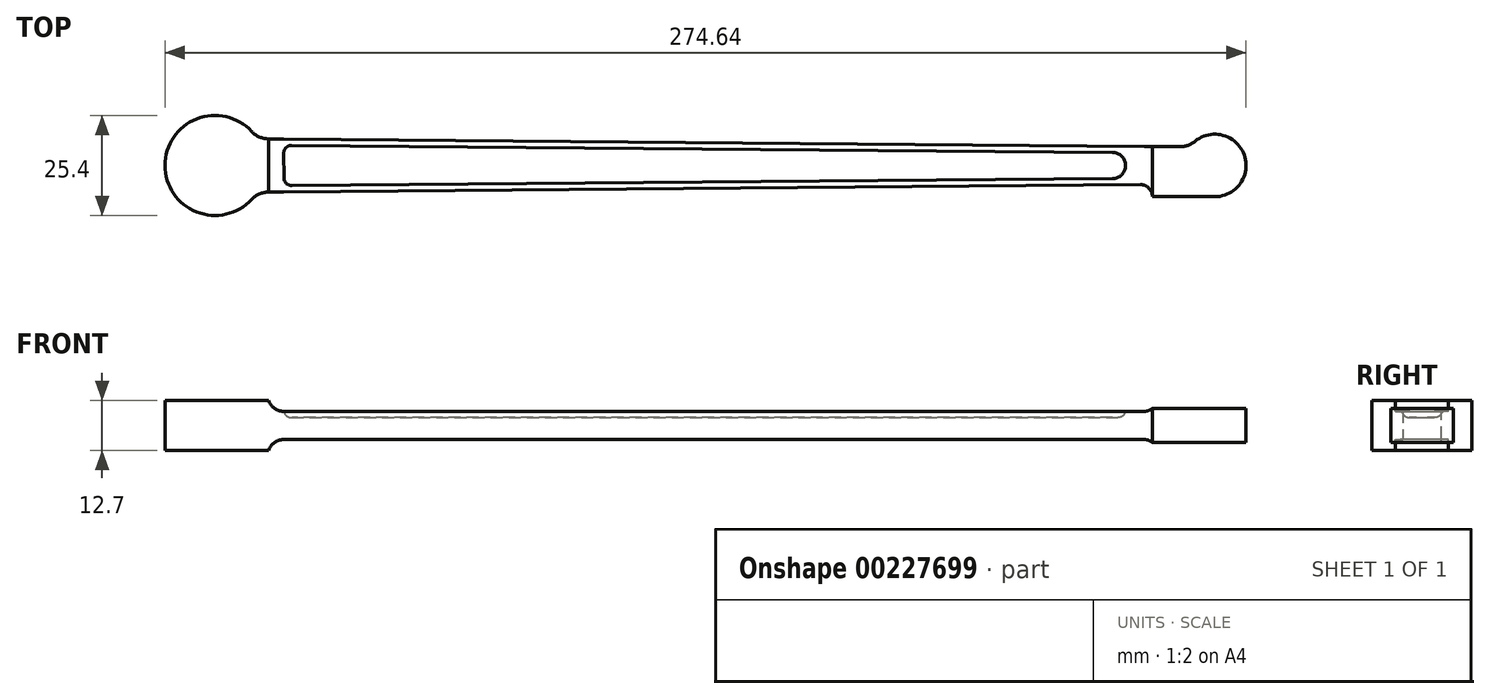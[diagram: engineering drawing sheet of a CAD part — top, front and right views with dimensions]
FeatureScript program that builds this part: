
annotation { "Feature Type Name" : "Feature", "Feature Type Description" : "" }
export const myFeature = defineFeature(function(context is Context, id is Id, definition is map)
    precondition{}
    {
        {
            var Q0;
            Q0=qCreatedBy(makeId("Top.planeOp"),FACE);
            var sketch = newSketch(context, id + "F0", { "sketchPlane" : qUnion([Q0])});
            skLineSegment(sketch, "E0", {"start": v(-127, 0) * mm, "end": v(127, 0) * mm, "construction": true});
            skArc(sketch, "E1", {"start": v(-117.7, 8.66) * mm, "mid": v(-139.7, 0) * mm, "end": v(-117.7, -8.66) * mm});
            skArc(sketch, "E2", {"start": v(127, -7.94) * mm, "mid": v(134.48, 2.67) * mm, "end": v(121.97, 6.14) * mm});
            skLineSegment(sketch, "E3", {"start": v(-113.37, 6.75) * mm, "end": v(118.12, 4.78) * mm});
            skLineSegment(sketch, "E4", {"start": v(-113.37, -6.75) * mm, "end": v(108.1, -4.87) * mm});
            skArc(sketch, "E5", {"start": v(-117.7, 8.66) * mm, "mid": v(-115.73, 7.26) * mm, "end": v(-113.37, 6.75) * mm});
            skArc(sketch, "E6", {"start": v(-113.37, -6.75) * mm, "mid": v(-115.73, -7.26) * mm, "end": v(-117.7, -8.66) * mm});
            skLineSegment(sketch, "E7", {"start": v(127, -7.94) * mm, "end": v(111.12, -7.94) * mm});
            skArc(sketch, "E8", {"start": v(111.13, -7.87) * mm, "mid": v(110.24, -5.74) * mm, "end": v(108.1, -4.87) * mm});
            skLineSegment(sketch, "E9", {"start": v(111.12, -7.87) * mm, "end": v(111.12, -7.94) * mm});
            skLineSegment(sketch, "E10", {"start": v(111.12, -7.87) * mm, "end": v(111.12, 4.84) * mm});
            skLineSegment(sketch, "E11", {"start": v(-113.37, 6.75) * mm, "end": v(-113.37, -6.75) * mm});
            skPoint(sketch, "E12.orphan", {"position": v(120.65, -4.76) * mm});
            skPoint(sketch, "E13.orphan", {"position": v(-116.26, 6.77) * mm});
            skPoint(sketch, "E14.orphan", {"position": v(-116.26, -6.77) * mm});
            skPoint(sketch, "E15.visualSharp", {"position": v(120.65, 4.76) * mm});
            skArc(sketch, "E15.filletArc", {"start": v(118.12, 4.78) * mm, "mid": v(120.16, 5.12) * mm, "end": v(121.97, 6.14) * mm});
            skSolve(sketch);
        }
        {
            var Q0;
            Q0=qSketchRegion(id+"F0",true);
            extrude(context, id + "F1", {"entities" : qUnion([Q0]), "endBound" : BoundingType.SYMMETRIC, "depth" : 7.14 * mm});
        }
        {
            var Q0;
            {var subQ0=sQuery(id+"F0.wireOp",EDGE,"E1");var subQ1=makeQuery(id+"F0.imprint","INTERSECT",VERTEX,{"derivedFrom":[subQ0,sQuery(id+"F0.wireOp",EDGE,"E3")]});Q0=makeQuery(id+"F0.imprint","IMPRINT",FACE,{"disambiguationData":[TD([[makeQuery(id+"F0.imprint","IMPRINT",EDGE,{"disambiguationData":[TD([[subQ1,-1.0]])],"derivedFrom":subQ0}),1.0]])]});}
            extrude(context, id + "F2", {"entities" : qUnion([Q0]), "operationType" : NewBodyOperationType.ADD, "endBound" : BoundingType.SYMMETRIC, "depth" : 12.7 * mm});
        }
        {
            var Q0;
            Q0=makeQuery(id+"F0.imprint","IMPRINT",FACE,{"disambiguationData":[TD([[makeQuery(id+"F0.imprint","IMPRINT",EDGE,{"derivedFrom":sQuery(id+"F0.wireOp",EDGE,"E2")}),1.0]])]});
            extrude(context, id + "F3", {"entities" : qUnion([Q0]), "operationType" : NewBodyOperationType.ADD, "endBound" : BoundingType.SYMMETRIC, "depth" : 8.73 * mm});
        }
        {
            var Q0;
            Q0=makeQuery(id+"F2.boolean.opBoolean","INTERSECT",EDGE,{"derivedFrom":[makeQuery(id+"F1.opExtrude","CAP_FACE",FACE,{"disambiguationData":[OSD([sQuery(id+"F0.wireOp",EDGE,"E1"),sQuery(id+"F0.wireOp",EDGE,"E2"),sQuery(id+"F0.wireOp",EDGE,"E3"),sQuery(id+"F0.wireOp",EDGE,"E4"),sQuery(id+"F0.wireOp",EDGE,"E5"),sQuery(id+"F0.wireOp",EDGE,"E6"),sQuery(id+"F0.wireOp",EDGE,"E7"),sQuery(id+"F0.wireOp",EDGE,"E8"),sQuery(id+"F0.wireOp",EDGE,"E9"),sQuery(id+"F0.wireOp",EDGE,"E15.filletArc")])],"isStart":false}),makeQuery(id+"F2.opExtrude","SWEPT_FACE",FACE,{"disambiguationData":[OSD([sQuery(id+"F0.wireOp",EDGE,"E11")])]})]});
            var Q1;
            Q1=makeQuery(id+"F2.boolean.opBoolean","INTERSECT",EDGE,{"derivedFrom":[makeQuery(id+"F1.opExtrude","CAP_FACE",FACE,{"disambiguationData":[OSD([sQuery(id+"F0.wireOp",EDGE,"E1"),sQuery(id+"F0.wireOp",EDGE,"E2"),sQuery(id+"F0.wireOp",EDGE,"E3"),sQuery(id+"F0.wireOp",EDGE,"E4"),sQuery(id+"F0.wireOp",EDGE,"E5"),sQuery(id+"F0.wireOp",EDGE,"E6"),sQuery(id+"F0.wireOp",EDGE,"E7"),sQuery(id+"F0.wireOp",EDGE,"E8"),sQuery(id+"F0.wireOp",EDGE,"E9"),sQuery(id+"F0.wireOp",EDGE,"E15.filletArc")])],"isStart":true}),makeQuery(id+"F2.opExtrude","SWEPT_FACE",FACE,{"disambiguationData":[OSD([sQuery(id+"F0.wireOp",EDGE,"E11")])]})]});
            fillet(context, id + "F4", {"entities" : qUnion([Q0, Q1]), "radius" : 4 * mm, "tangentPropagation" : true, "allowEdgeOverflow" : false});
        }
        {
            var Q0;
            {var subQ0=sQuery(id+"F0.wireOp",EDGE,"E9");Q0=makeQuery(id+"F3.boolean.opBoolean","INTERSECT",EDGE,{"derivedFrom":[makeQuery(id+"F1.opExtrude","CAP_FACE",FACE,{"disambiguationData":[OSD([sQuery(id+"F0.wireOp",EDGE,"E1"),sQuery(id+"F0.wireOp",EDGE,"E2"),sQuery(id+"F0.wireOp",EDGE,"E3"),sQuery(id+"F0.wireOp",EDGE,"E4"),sQuery(id+"F0.wireOp",EDGE,"E5"),sQuery(id+"F0.wireOp",EDGE,"E6"),sQuery(id+"F0.wireOp",EDGE,"E7"),sQuery(id+"F0.wireOp",EDGE,"E8"),subQ0,sQuery(id+"F0.wireOp",EDGE,"E15.filletArc")])],"isStart":true}),makeQuery(id+"F3.opExtrude","SWEPT_FACE",FACE,{"disambiguationData":[OSD([subQ0,sQuery(id+"F0.wireOp",EDGE,"E10")])]})]});}
            var Q1;
            {var subQ0=sQuery(id+"F0.wireOp",EDGE,"E9");Q1=makeQuery(id+"F3.boolean.opBoolean","INTERSECT",EDGE,{"derivedFrom":[makeQuery(id+"F1.opExtrude","CAP_FACE",FACE,{"disambiguationData":[OSD([sQuery(id+"F0.wireOp",EDGE,"E1"),sQuery(id+"F0.wireOp",EDGE,"E2"),sQuery(id+"F0.wireOp",EDGE,"E3"),sQuery(id+"F0.wireOp",EDGE,"E4"),sQuery(id+"F0.wireOp",EDGE,"E5"),sQuery(id+"F0.wireOp",EDGE,"E6"),sQuery(id+"F0.wireOp",EDGE,"E7"),sQuery(id+"F0.wireOp",EDGE,"E8"),subQ0,sQuery(id+"F0.wireOp",EDGE,"E15.filletArc")])],"isStart":false}),makeQuery(id+"F3.opExtrude","SWEPT_FACE",FACE,{"disambiguationData":[OSD([subQ0,sQuery(id+"F0.wireOp",EDGE,"E10")])]})]});}
            fillet(context, id + "F5", {"entities" : qUnion([Q0, Q1]), "radius" : 3 * mm, "tangentPropagation" : true, "allowEdgeOverflow" : false});
        }
        {
            var Q0;
            Q0=makeQuery(id+"F1.opExtrude","CAP_FACE",FACE,{"disambiguationData":[OSD([sQuery(id+"F0.wireOp",EDGE,"E1"),sQuery(id+"F0.wireOp",EDGE,"E2"),sQuery(id+"F0.wireOp",EDGE,"E3"),sQuery(id+"F0.wireOp",EDGE,"E4"),sQuery(id+"F0.wireOp",EDGE,"E5"),sQuery(id+"F0.wireOp",EDGE,"E6"),sQuery(id+"F0.wireOp",EDGE,"E7"),sQuery(id+"F0.wireOp",EDGE,"E8"),sQuery(id+"F0.wireOp",EDGE,"E9"),sQuery(id+"F0.wireOp",EDGE,"E15.filletArc")])],"isStart":false});
            var sketch = newSketch(context, id + "F6", { "sketchPlane" : qUnion([Q0])});
            skLineSegment(sketch, "E16", {"start": v(101, -3.34) * mm, "end": v(-107.46, -5.1) * mm});
            skLineSegment(sketch, "E17", {"start": v(-109.48, -3.13) * mm, "end": v(-109.53, 3.1) * mm});
            skLineSegment(sketch, "E18", {"start": v(-107.51, 5.1) * mm, "end": v(101, 3.34) * mm});
            skArc(sketch, "E19", {"start": v(101, -3.34) * mm, "mid": v(104.3, 0) * mm, "end": v(101, 3.34) * mm});
            skPoint(sketch, "E20.visualSharp", {"position": v(-109.46, -5.13) * mm});
            skArc(sketch, "E20.filletArc", {"start": v(-109.48, -3.13) * mm, "mid": v(-108.88, -4.54) * mm, "end": v(-107.46, -5.1) * mm});
            skPoint(sketch, "E21.visualSharp", {"position": v(-109.55, 5.13) * mm});
            skArc(sketch, "E21.filletArc", {"start": v(-107.51, 5.1) * mm, "mid": v(-108.94, 4.52) * mm, "end": v(-109.53, 3.1) * mm});
            skSolve(sketch);
        }
        {
            var Q0;
            Q0 = qSketchRegion(id + "F6", true);
            extrude(context, id + "F7", {"entities" : qUnion([Q0]), "operationType" : NewBodyOperationType.REMOVE, "oppositeDirection" : true, "depth" : 1.59 * mm});
        }
        {
            var Q0;
            Q0=makeQuery(id+"F7.boolean.opBoolean","COPY",EDGE,{"derivedFrom":makeQuery(id+"F7.opExtrude","CAP_EDGE",EDGE,{"disambiguationData":[OSD([sQuery(id+"F6.wireOp",EDGE,"E16")])],"isStart":false})});
            fillet(context, id + "F8", {"entities" : qUnion([Q0]), "radius" : 2 * mm, "tangentPropagation" : true, "allowEdgeOverflow" : false});
        }
    });
